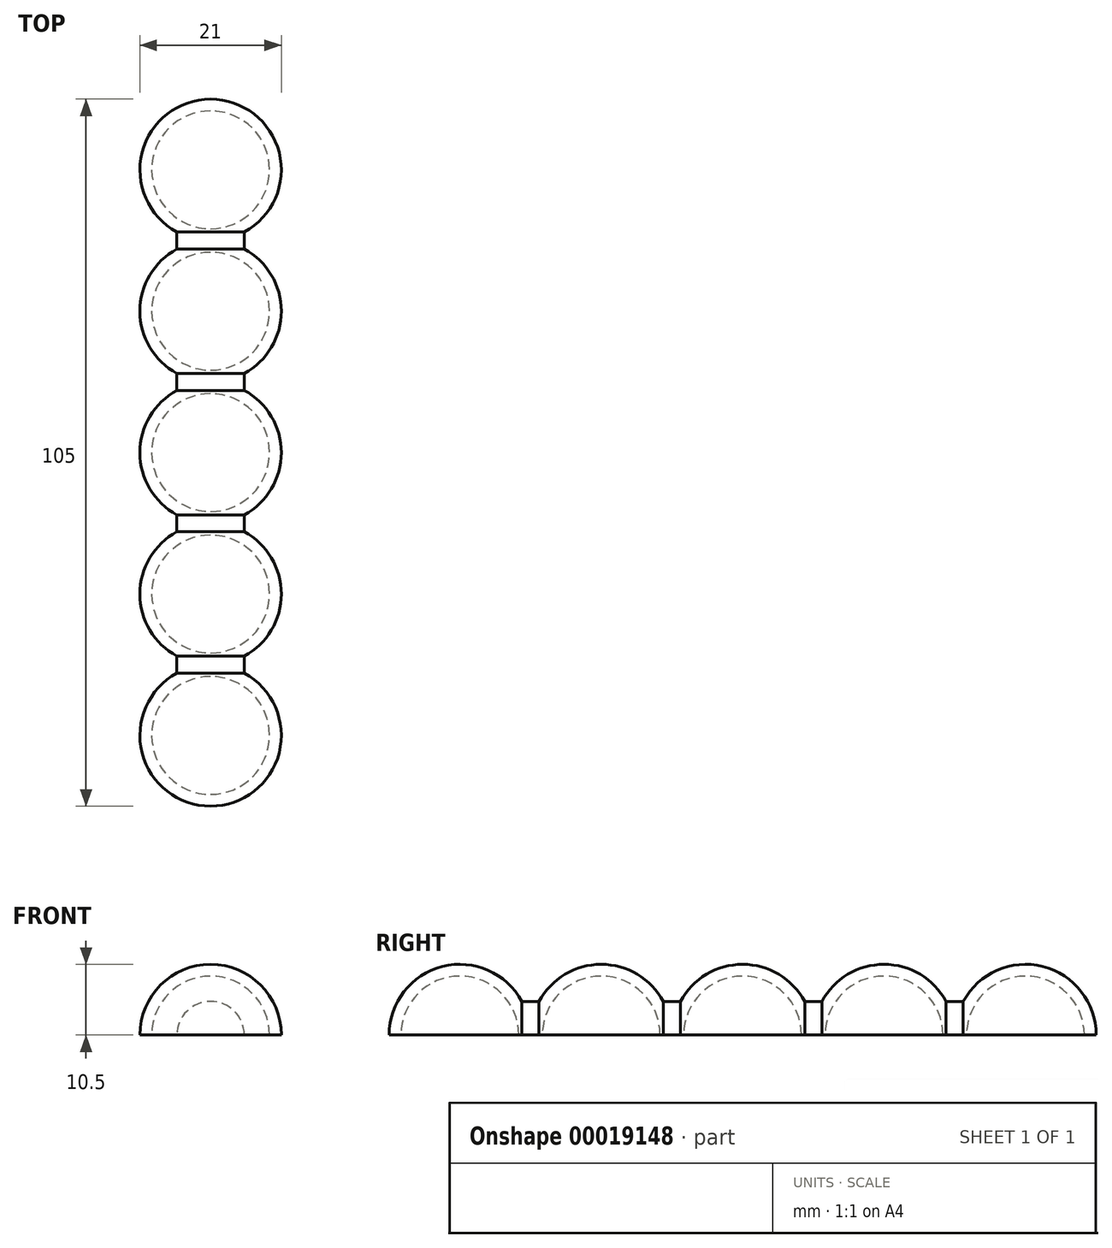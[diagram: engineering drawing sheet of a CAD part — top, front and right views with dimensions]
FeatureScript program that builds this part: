
annotation { "Feature Type Name" : "Feature", "Feature Type Description" : "" }
export const myFeature = defineFeature(function(context is Context, id is Id, definition is map)
    precondition{}
    {
        {
            var Q0;
            Q0=qCreatedBy(makeId("Top.planeOp"),FACE);
            var sketch = newSketch(context, id + "F0", { "sketchPlane" : qUnion([Q0])});
            skArc(sketch, "E0", {"start": v(0, -10.5) * mm, "mid": v(10.5, 0) * mm, "end": v(0, 10.5) * mm});
            skArc(sketch, "E1.0.1.0", {"start": v(0, 10.5) * mm, "mid": v(10.5, 21) * mm, "end": v(0, 31.5) * mm});
            skArc(sketch, "E1.0.2.0", {"start": v(0, 31.5) * mm, "mid": v(10.5, 42) * mm, "end": v(0, 52.5) * mm});
            skArc(sketch, "E1.0.3.0", {"start": v(0, 52.5) * mm, "mid": v(10.5, 63) * mm, "end": v(0, 73.5) * mm});
            skArc(sketch, "E1.0.4.0", {"start": v(0, 73.5) * mm, "mid": v(10.5, 84) * mm, "end": v(0, 94.5) * mm});
            skLineSegment(sketch, "E1.direction1", {"start": v(0, 0) * mm, "end": v(25, 0) * mm, "construction": true});
            skLineSegment(sketch, "E1.direction2", {"start": v(0, 0) * mm, "end": v(0, 21) * mm, "construction": true});
            skArc(sketch, "E2", {"start": v(0, -8.75) * mm, "mid": v(8.75, 0) * mm, "end": v(0, 8.75) * mm});
            skArc(sketch, "E3.0.1.0", {"start": v(0, 12.25) * mm, "mid": v(8.75, 21) * mm, "end": v(0, 29.75) * mm});
            skArc(sketch, "E3.0.2.0", {"start": v(0, 33.25) * mm, "mid": v(8.75, 42) * mm, "end": v(0, 50.75) * mm});
            skArc(sketch, "E3.0.3.0", {"start": v(0, 54.25) * mm, "mid": v(8.75, 63) * mm, "end": v(0, 71.75) * mm});
            skArc(sketch, "E3.0.4.0", {"start": v(0, 75.25) * mm, "mid": v(8.75, 84) * mm, "end": v(0, 92.75) * mm});
            skLineSegment(sketch, "E4", {"start": v(0, -10.5) * mm, "end": v(0, -8.75) * mm});
            skLineSegment(sketch, "E5.trimOffspring", {"start": v(0, 8.75) * mm, "end": v(0, 12.25) * mm});
            skLineSegment(sketch, "E6.trimOffspring", {"start": v(0, 29.75) * mm, "end": v(0, 33.25) * mm});
            skLineSegment(sketch, "E7.trimOffspring", {"start": v(0, 50.75) * mm, "end": v(0, 54.25) * mm});
            skLineSegment(sketch, "E8.trimOffspring", {"start": v(0, 71.75) * mm, "end": v(0, 75.25) * mm});
            skLineSegment(sketch, "E9.trimOffspring", {"start": v(0, 92.75) * mm, "end": v(0, 94.5) * mm});
            skLineSegment(sketch, "E10", {"start": v(5, 74.77) * mm, "end": v(5, 72.23) * mm});
            skLineSegment(sketch, "E11.trimOffspring", {"start": v(5, 11.77) * mm, "end": v(5, 9.23) * mm});
            skLineSegment(sketch, "E12.trimOffspring", {"start": v(5, 32.77) * mm, "end": v(5, 30.23) * mm});
            skLineSegment(sketch, "E13.trimOffspring", {"start": v(5, 53.77) * mm, "end": v(5, 51.23) * mm});
            skLineSegment(sketch, "E14", {"start": v(0, -10.5) * mm, "end": v(0, -15.48) * mm});
            skSolve(sketch);
        }
        {
            var Q0;
            {var subQ0=sQuery(id+"F0.wireOp",EDGE,"E2");Q0=makeQuery(id+"F0.imprint","IMPRINT",FACE,{"disambiguationData":[TD([[makeQuery(id+"F0.imprint","IMPRINT",EDGE,{"derivedFrom":subQ0}),-1.0]])]});}
            var Q1;
            {var subQ0=sQuery(id+"F0.wireOp",EDGE,"E3.0.1.0");Q1=makeQuery(id+"F0.imprint","IMPRINT",FACE,{"disambiguationData":[TD([[makeQuery(id+"F0.imprint","IMPRINT",EDGE,{"derivedFrom":subQ0}),-1.0]])]});}
            var Q2;
            {var subQ3=sQuery(id+"F0.wireOp",EDGE,"E11.trimOffspring");Q2=makeQuery(id+"F0.imprint","IMPRINT",FACE,{"disambiguationData":[TD([[makeQuery(id+"F0.imprint","IMPRINT",EDGE,{"derivedFrom":subQ3}),-1.0]])]});}
            var Q3;
            {var subQ0=sQuery(id+"F0.wireOp",EDGE,"E3.0.2.0");Q3=makeQuery(id+"F0.imprint","IMPRINT",FACE,{"disambiguationData":[TD([[makeQuery(id+"F0.imprint","IMPRINT",EDGE,{"derivedFrom":subQ0}),-1.0]])]});}
            var Q4;
            {var subQ3=sQuery(id+"F0.wireOp",EDGE,"E12.trimOffspring");Q4=makeQuery(id+"F0.imprint","IMPRINT",FACE,{"disambiguationData":[TD([[makeQuery(id+"F0.imprint","IMPRINT",EDGE,{"derivedFrom":subQ3}),-1.0]])]});}
            var Q5;
            {var subQ0=sQuery(id+"F0.wireOp",EDGE,"E3.0.3.0");Q5=makeQuery(id+"F0.imprint","IMPRINT",FACE,{"disambiguationData":[TD([[makeQuery(id+"F0.imprint","IMPRINT",EDGE,{"derivedFrom":subQ0}),-1.0]])]});}
            var Q6;
            {var subQ3=sQuery(id+"F0.wireOp",EDGE,"E13.trimOffspring");Q6=makeQuery(id+"F0.imprint","IMPRINT",FACE,{"disambiguationData":[TD([[makeQuery(id+"F0.imprint","IMPRINT",EDGE,{"derivedFrom":subQ3}),-1.0]])]});}
            var Q7;
            {var subQ0=sQuery(id+"F0.wireOp",EDGE,"E3.0.4.0");Q7=makeQuery(id+"F0.imprint","IMPRINT",FACE,{"disambiguationData":[TD([[makeQuery(id+"F0.imprint","IMPRINT",EDGE,{"derivedFrom":subQ0}),-1.0]])]});}
            var Q8;
            {var subQ3=sQuery(id+"F0.wireOp",EDGE,"E10");Q8=makeQuery(id+"F0.imprint","IMPRINT",FACE,{"disambiguationData":[TD([[makeQuery(id+"F0.imprint","IMPRINT",EDGE,{"derivedFrom":subQ3}),-1.0]])]});}
            var Q9;
            Q9=sQuery(id+"F0.wireOp",EDGE,"E14");
            revolve(context, id + "F1", {"entities" : qUnion([Q0, Q1, Q2, Q3, Q4, Q5, Q6, Q7, Q8]), "axis" : qUnion([Q9]), "revolveType" : RevolveType.ONE_DIRECTION, "angle" : 180 * degree});
        }
    });
